# Revit family: NLRS_57_DUF_UN_rechthoekige-mitred-stuts_nijburg
name_source: partatom
category: Duct Fittings
units: mm (PartAtom-declared; Revit-internal decimal feet)

## family parameters
Always vertical = Yes
Cut with Voids When Loaded = No
OmniClass Number = 23.75.70.14
OmniClass Title = Air Ductwork
Part Type = Tap - Adjustable
Round Connector Dimension = Use Diameter
Shared = No
Work Plane-Based = No

## types (1)
- Rechthoekige stuts, mitred
    Assembly Code = 57.70
    Default Elevation = 0 mm  [stored 0 ft]
    Description = Rechthoekige mitred stuts op recht kanaal
    Manufacturer = Nijburg Products
    Model = Rechthoekige aftakking
    NLRS_C_content_datum_gewijzigd = 10-05-2023
    NLRS_C_content_provider = Nijburg Klimaattechniek
    NLRS_C_content_versie = 1.20.00
    NLRS_C_description = Rechthoekige mitred stuts op recht kanaal
    NLRS_C_model = Rechthoekige aftakking
    NPR_Dummy = 1
    URL = https://nijburg-klimaattechniek.nl

note: [stored X ft] marks values corroborated as IEEE doubles in the binary element streams (Revit-internal decimal feet)

## geometry (parser evidence)
native form markers: Sweep x4
no freeform markers — native parametric forms only
